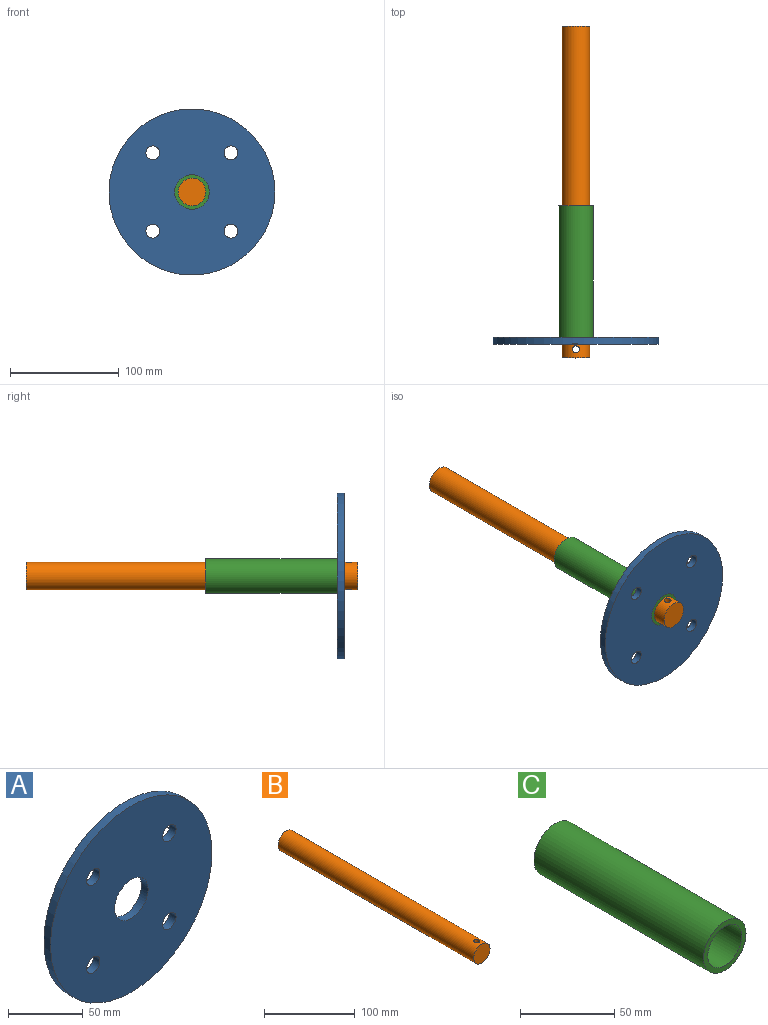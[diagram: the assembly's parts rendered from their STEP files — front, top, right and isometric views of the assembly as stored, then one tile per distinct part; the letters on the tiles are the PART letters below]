
ASSEMBLY  parts=3 mates=2
PART A: 8 faces, bbox 152.4x6.4x152.4 mm
  f0: cylinder r=76.2mm len=152.4mm, axis (0,1,0), area 3040.2mm2, adj f6,f7
  f1: cylinder r=15.88mm len=31.75mm, axis (0,1,0), area 633.4mm2, adj f6,f7
  f2: cylinder r=6.35mm len=12.7mm, axis (0,1,0), area 253.4mm2, adj f6,f7
  f3: cylinder r=6.35mm len=12.7mm, axis (0,1,0), area 253.4mm2, adj f6,f7
  f4: cylinder r=6.35mm len=12.7mm, axis (0,1,0), area 253.4mm2, adj f6,f7
  f5: cylinder r=6.35mm len=12.7mm, axis (0,1,0), area 253.4mm2, adj f6,f7
  f6: plane 152.4x152.4mm, normal (0,-1,0), area 16943mm2, adj f0,f1,f2,f3,f4,f5
  f7: plane 152.4x152.4mm, normal (0,1,0), area 16943mm2, adj f0,f1,f2,f3,f4,f5
PART B: 4 faces, bbox 25.4x304.8x25.4 mm
  f0: cylinder r=12.7mm len=304.8mm, axis (0,1,0), area 24258.1mm2, adj f1,f2,f3
  f1: plane 25.4x25.4mm, normal (0,-1,0), area 506.7mm2, adj f0
  f2: plane 25.4x25.4mm, normal (0,1,0), area 506.7mm2, adj f0
  f3: cylinder r=3.17mm len=25.4mm, axis (0,0,1), area 498.7mm2, adj f0
PART C: 4 faces, bbox 31.8x127x31.8 mm
  f0: cylinder r=12.7mm len=127mm, axis (0,1,0), area 10134.1mm2, adj f2,f3
  f1: cylinder r=15.88mm len=127mm, axis (0,1,0), area 12667.7mm2, adj f2,f3
  f2: plane 31.75x31.75mm, normal (0,-1,0), area 285mm2, adj f0,f1
  f3: plane 31.75x31.75mm, normal (0,1,0), area 285mm2, adj f0,f1
PLACE A rot(axis=(1,0,0),180deg) t=(-103.12,-229.3,-45.09)mm
PLACE B t=(-103.12,62.8,-45.09)mm fixed
PLACE C rot(axis=(1,0,0),180deg) t=(-103.12,-229.3,-45.09)mm
MATE fastened C.f0 <-> A.f0  axis (0,-1,0) through (-103.12,-229.3,-45.09)mm
MATE revolute A.f0 <-> B.f0  axis (0,-1,0) through (-103.12,-229.3,-45.09)mm
